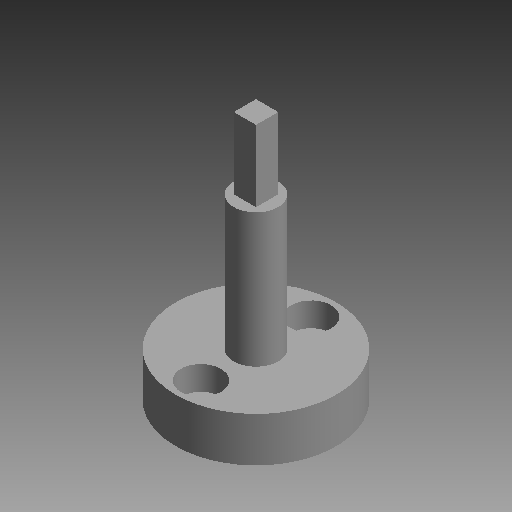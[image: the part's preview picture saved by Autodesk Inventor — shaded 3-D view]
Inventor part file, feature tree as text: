
AUTODESK INVENTOR PART (.ipt)
format: ipt  version: 2019 (Build 230136000, 136)  size: 88,064 bytes
history: native  units: mm (DEFAULTED — no unit token found)
features: sketch x4, other x3
ambient origin geometry x8: Origin, YZ Plane, XZ Plane, XY Plane, X Axis, Y Axis, Z Axis, Center Point
bodies: Solid1 (feature_tree)
feature tree (7):
  other  "vex motor adaptor to tetrix.ipt"
  other  "Solid1::vex motor adaptor to tetrix.ipt"
  other  "TaggingFeature1"
  sketch  "Sketch1"  dims[d0=10.0mm]
  sketch  "Sketch2"
  sketch  "Sketch3"
  sketch  "Sketch4"
